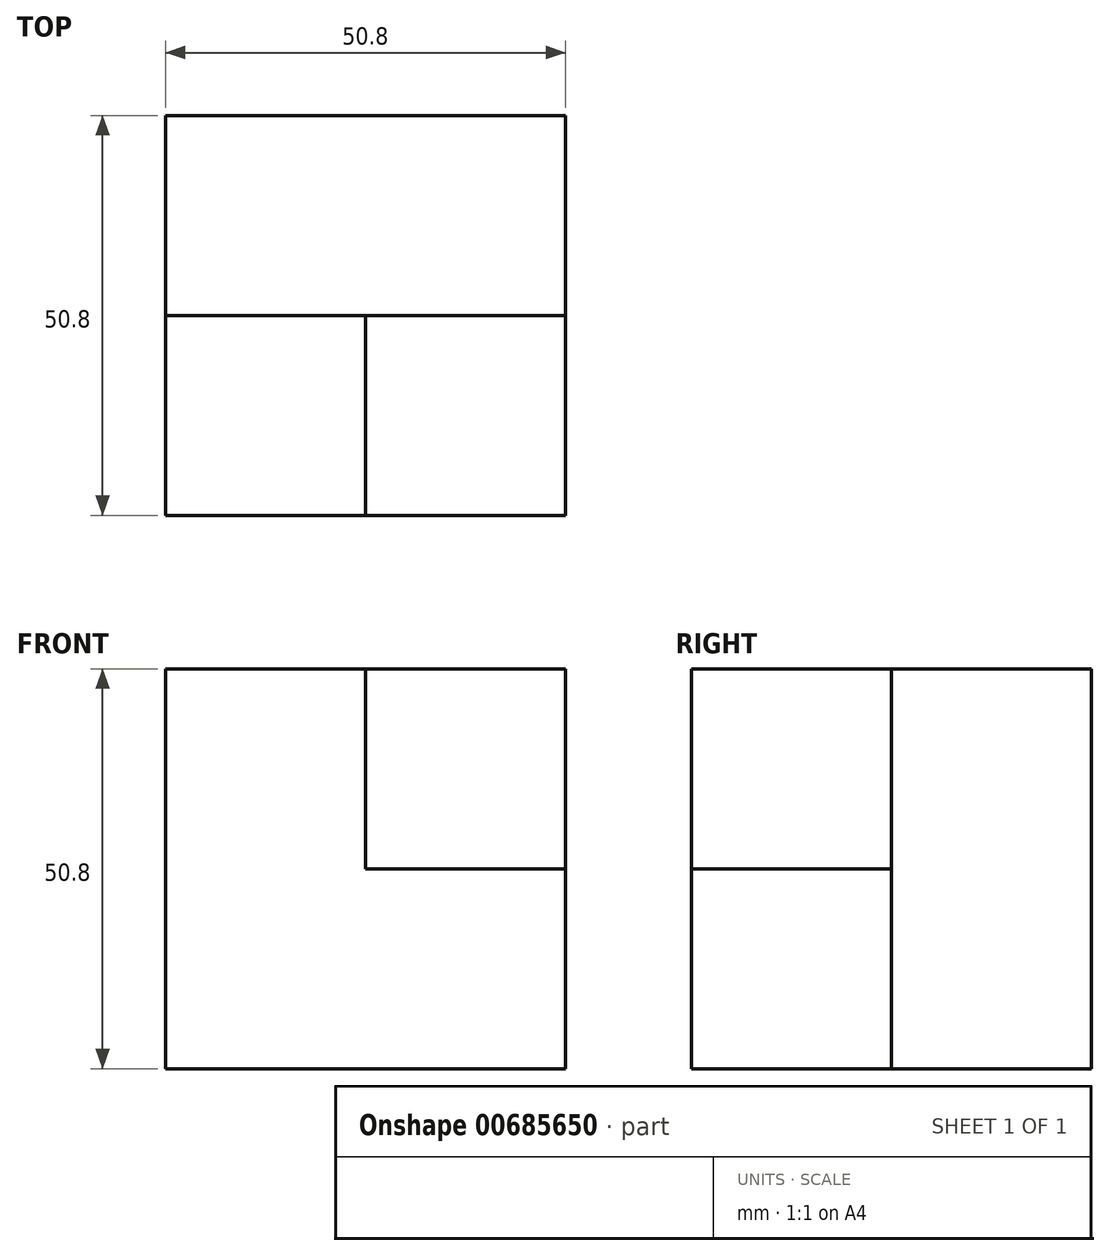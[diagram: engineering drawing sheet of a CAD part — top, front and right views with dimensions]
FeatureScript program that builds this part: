
annotation { "Feature Type Name" : "Feature", "Feature Type Description" : "" }
export const myFeature = defineFeature(function(context is Context, id is Id, definition is map)
    precondition{}
    {
        {
            var Q0;
            Q0=qCreatedBy(makeId("Front.planeOp"),FACE);
            var sketch = newSketch(context, id + "F0", { "sketchPlane" : qUnion([Q0])});
            skLineSegment(sketch, "E0.bottom", {"start": v(0, 0) * mm, "end": v(-50.8, 0) * mm});
            skLineSegment(sketch, "E0.top", {"start": v(0, 0) * mm, "end": v(-50.8, 0) * mm});
            skLineSegment(sketch, "E0.left", {"start": v(0, 0) * mm, "end": v(0, 0) * mm});
            skLineSegment(sketch, "E0.right", {"start": v(-50.8, 0) * mm, "end": v(-50.8, 0) * mm});
            skLineSegment(sketch, "E1.top", {"start": v(0, 50.8) * mm, "end": v(0, 50.8) * mm});
            skLineSegment(sketch, "E1.left", {"start": v(0, 0) * mm, "end": v(0, 50.8) * mm});
            skLineSegment(sketch, "E1.right", {"start": v(0, 0) * mm, "end": v(0, 50.8) * mm});
            skLineSegment(sketch, "E2.bottom", {"start": v(0, 50.8) * mm, "end": v(-50.37, 50.8) * mm});
            skLineSegment(sketch, "E2.top", {"start": v(0, 50.8) * mm, "end": v(-50.37, 50.8) * mm});
            skLineSegment(sketch, "E2.right", {"start": v(-50.37, 50.8) * mm, "end": v(-50.37, 50.8) * mm});
            skLineSegment(sketch, "E3.bottom", {"start": v(-50.37, 50.8) * mm, "end": v(-50.8, 50.8) * mm});
            skLineSegment(sketch, "E3.top", {"start": v(-50.37, 0) * mm, "end": v(-50.8, 0) * mm});
            skLineSegment(sketch, "E3.left", {"start": v(-50.37, 50.8) * mm, "end": v(-50.37, 0) * mm});
            skLineSegment(sketch, "E3.right", {"start": v(-50.8, 50.8) * mm, "end": v(-50.8, 0) * mm});
            skSolve(sketch);
        }
        {
            var Q0;
            Q0 = qSketchRegion(id + "F0", true);
            extrude(context, id + "F1", {"entities" : qUnion([Q0]), "depth" : 25.4 * mm, "offsetDistance" : 25.4 * mm});
        }
        {
            var Q0;
            Q0=makeQuery(id+"F1.opExtrude","CAP_FACE",FACE,{"disambiguationData":[OSD([sQuery(id+"F0.wireOp",EDGE,"E0.top"),sQuery(id+"F0.wireOp",EDGE,"E1.right"),sQuery(id+"F0.wireOp",EDGE,"E2.top"),sQuery(id+"F0.wireOp",EDGE,"E3.bottom"),sQuery(id+"F0.wireOp",EDGE,"E3.top"),sQuery(id+"F0.wireOp",EDGE,"E3.right")])],"isStart":false});
            var sketch = newSketch(context, id + "F2", { "sketchPlane" : qUnion([Q0])});
            skSolve(sketch);
        }
        {
            var Q0;
            Q0 = qSketchRegion(id + "F2", true);
            var Q1;
            Q1=makeQuery(id+"F2.imprint","IMPRINT",FACE,{"disambiguationData":[TD([[makeQuery(id+"F2.imprint","IMPRINT",EDGE,{"derivedFrom":makeQuery(id+"F1.opExtrude","CAP_EDGE",EDGE,{"disambiguationData":[OSD([sQuery(id+"F0.wireOp",EDGE,"E1.right")])],"isStart":false})}),1.0]])]});
            var Q2;
            Q2=makeQuery(id+"F1.opExtrude","SWEPT_FACE",FACE,{"disambiguationData":[OSD([sQuery(id+"F0.wireOp",EDGE,"E1.right")])]});
            var Q3;
            Q3=makeQuery(id+"F1.opExtrude","CAP_FACE",FACE,{"disambiguationData":[OSD([sQuery(id+"F0.wireOp",EDGE,"E0.top"),sQuery(id+"F0.wireOp",EDGE,"E1.right"),sQuery(id+"F0.wireOp",EDGE,"E2.top"),sQuery(id+"F0.wireOp",EDGE,"E3.bottom"),sQuery(id+"F0.wireOp",EDGE,"E3.top"),sQuery(id+"F0.wireOp",EDGE,"E3.right")])],"isStart":false});
            var Q4;
            Q4=makeQuery(id+"F1.opExtrude","SWEPT_FACE",FACE,{"disambiguationData":[OSD([sQuery(id+"F0.wireOp",EDGE,"E0.top"),sQuery(id+"F0.wireOp",EDGE,"E3.top")])]});
            var Q5;
            Q5=makeQuery(id+"F1.opExtrude","CAP_FACE",FACE,{"disambiguationData":[OSD([sQuery(id+"F0.wireOp",EDGE,"E0.top"),sQuery(id+"F0.wireOp",EDGE,"E1.right"),sQuery(id+"F0.wireOp",EDGE,"E2.top"),sQuery(id+"F0.wireOp",EDGE,"E3.bottom"),sQuery(id+"F0.wireOp",EDGE,"E3.top"),sQuery(id+"F0.wireOp",EDGE,"E3.right")])],"isStart":true});
            extrude(context, id + "F3", {"entities" : qUnion([Q0, Q1, Q2, Q3, Q4, Q5]), "depth" : 25.4 * mm, "offsetDistance" : 25.4 * mm});
        }
        {
            var Q0;
            Q0=makeQuery(id+"F1.opExtrude","CAP_FACE",FACE,{"disambiguationData":[OSD([sQuery(id+"F0.wireOp",EDGE,"E0.top"),sQuery(id+"F0.wireOp",EDGE,"E1.right"),sQuery(id+"F0.wireOp",EDGE,"E2.top"),sQuery(id+"F0.wireOp",EDGE,"E3.bottom"),sQuery(id+"F0.wireOp",EDGE,"E3.top"),sQuery(id+"F0.wireOp",EDGE,"E3.right")])],"isStart":false});
            var sketch = newSketch(context, id + "F4", { "sketchPlane" : qUnion([Q0])});
            skLineSegment(sketch, "E4", {"start": v(0, 0) * mm, "end": v(0, 25.4) * mm});
            skLineSegment(sketch, "E5", {"start": v(0, 25.4) * mm, "end": v(-25.4, 25.4) * mm});
            skLineSegment(sketch, "E6", {"start": v(-25.4, 25.4) * mm, "end": v(-25.4, 50.8) * mm});
            skLineSegment(sketch, "E7", {"start": v(-25.4, 50.8) * mm, "end": v(-50.8, 50.8) * mm});
            skLineSegment(sketch, "E8", {"start": v(-50.8, 50.8) * mm, "end": v(-50.8, 0) * mm});
            skLineSegment(sketch, "E9", {"start": v(-50.8, 0) * mm, "end": v(0, 0) * mm});
            skSolve(sketch);
        }
        {
            var Q0;
            Q0 = qSketchRegion(id + "F4", true);
            extrude(context, id + "F5", {"entities" : qUnion([Q0]), "depth" : 25.4 * mm, "offsetDistance" : 25.4 * mm});
        }
        {
            var Q0;
            Q0 = qSketchRegion(id + "F4", true);
            extrude(context, id + "F6", {"entities" : qUnion([Q0]), "depth" : 25.4 * mm, "offsetDistance" : 25.4 * mm});
        }
    });
